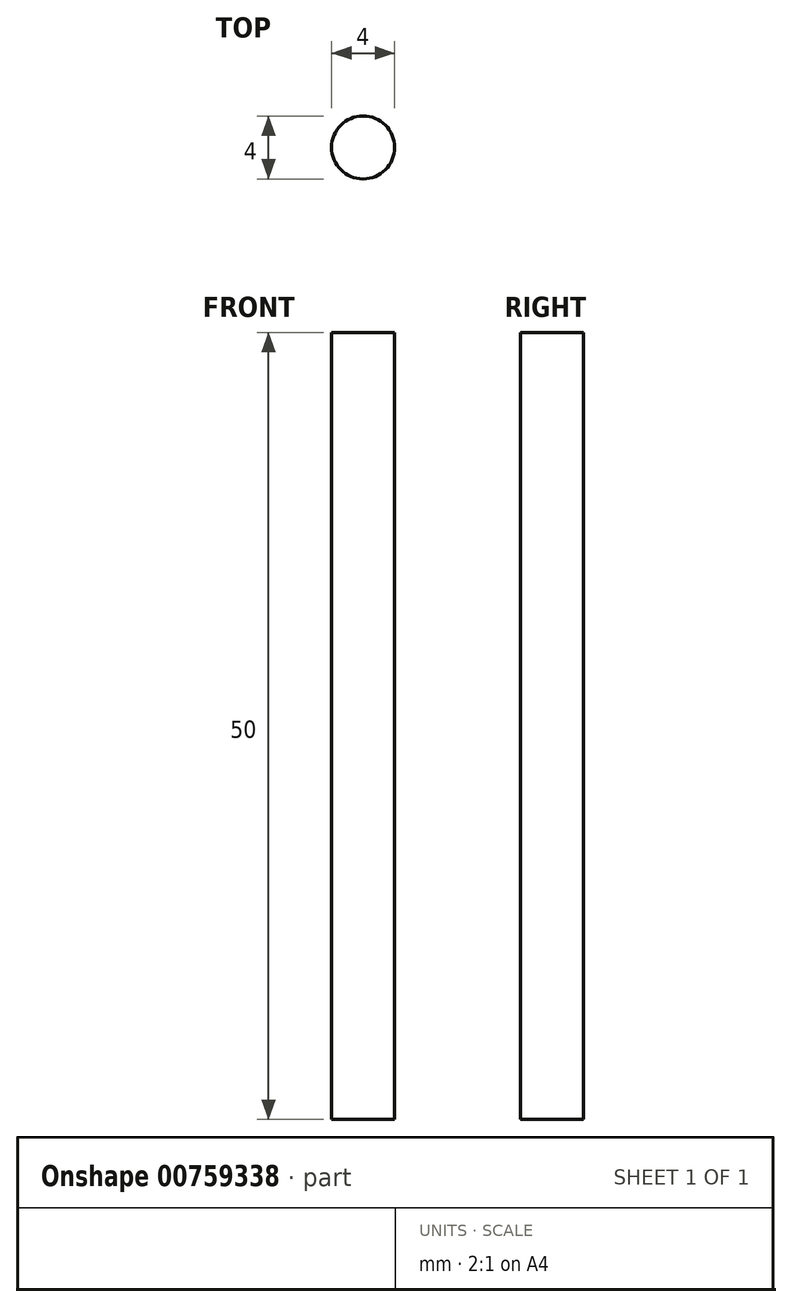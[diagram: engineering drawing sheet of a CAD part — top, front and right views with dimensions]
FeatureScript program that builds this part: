
annotation { "Feature Type Name" : "Feature", "Feature Type Description" : "" }
export const myFeature = defineFeature(function(context is Context, id is Id, definition is map)
    precondition{}
    {
        {
            var Q0;
            Q0=qCreatedBy(makeId("Top.planeOp"),FACE);
            var sketch = newSketch(context, id + "F0", { "sketchPlane" : qUnion([Q0])});
            skCircle(sketch, "E0", {"center": v(0, 0) * mm, "radius": 2 * mm});
            skSolve(sketch);
        }
        {
            var Q0;
            Q0 = qSketchRegion(id + "F0", true);
            extrude(context, id + "F1", {"entities" : qUnion([Q0]), "depth" : 50 * mm, "offsetDistance" : 25 * mm});
        }
    });
